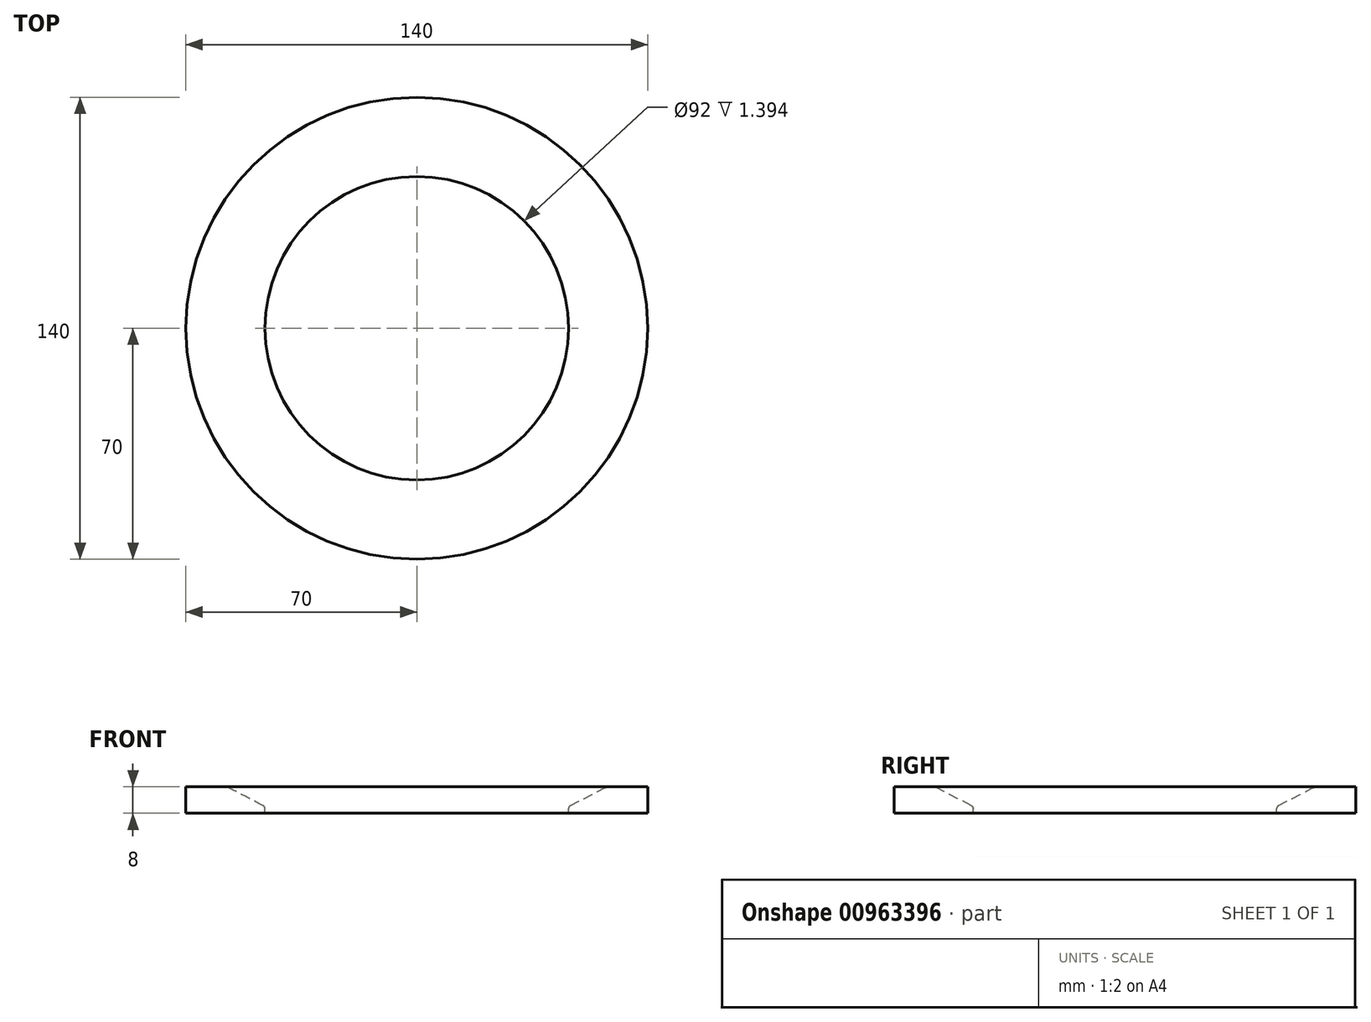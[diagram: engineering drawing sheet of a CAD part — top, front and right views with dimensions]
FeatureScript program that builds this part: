
annotation { "Feature Type Name" : "Feature", "Feature Type Description" : "" }
export const myFeature = defineFeature(function(context is Context, id is Id, definition is map)
    precondition{}
    {
        {
            var Q0;
            Q0=qCreatedBy(makeId("Front.planeOp"),FACE);
            var sketch = newSketch(context, id + "F0", { "sketchPlane" : qUnion([Q0])});
            skLineSegment(sketch, "E0", {"start": v(-70, 6) * mm, "end": v(-57.5, 6) * mm});
            skLineSegment(sketch, "E1", {"start": v(-46, 0) * mm, "end": v(-46, -2) * mm});
            skLineSegment(sketch, "E2", {"start": v(-57.5, 6) * mm, "end": v(-46, 0) * mm});
            skLineSegment(sketch, "E3", {"start": v(-46, -2) * mm, "end": v(-55, -2) * mm});
            skLineSegment(sketch, "E4", {"start": v(-70, 6) * mm, "end": v(-70, -2) * mm});
            skLineSegment(sketch, "E5", {"start": v(-55, -2) * mm, "end": v(-70, -2) * mm});
            skLineSegment(sketch, "E6", {"start": v(0, 61) * mm, "end": v(0, -54.93) * mm, "construction": true});
            skSolve(sketch);
        }
        {
            var Q0;
            Q0=makeQuery(id+"F0.imprint","IMPRINT",FACE,{"disambiguationData":[TD([[makeQuery(id+"F0.imprint","IMPRINT",EDGE,{"derivedFrom":sQuery(id+"F0.wireOp",EDGE,"E0")}),-1.0]])]});
            var Q1;
            Q1=sQuery(id+"F0.wireOp",EDGE,"E6");
            revolve(context, id + "F1", {"surfaceOperationType" : NewSurfaceOperationType.NEW, "entities" : qUnion([Q0]), "axis" : qUnion([Q1]), "revolveType" : RevolveType.FULL});
        }
        {
            var Q0;
            Q0=makeQuery(id+"F1.opRevolve","SWEPT_EDGE",EDGE,{"disambiguationData":[OSD([sQuery(id+"F0.wireOp",EDGE,"E0"),sQuery(id+"F0.wireOp",EDGE,"E2")])]});
            fillet(context, id + "F2", {"entities" : qUnion([Q0]), "radius" : 3 * mm, "tangentPropagation" : true, "allowEdgeOverflow" : false});
        }
        {
            var Q0;
            Q0=makeQuery(id+"F1.opRevolve","SWEPT_EDGE",EDGE,{"disambiguationData":[OSD([sQuery(id+"F0.wireOp",EDGE,"E1"),sQuery(id+"F0.wireOp",EDGE,"E2")])]});
            fillet(context, id + "F3", {"entities" : qUnion([Q0]), "radius" : 1 * mm, "tangentPropagation" : true, "allowEdgeOverflow" : false});
        }
    });
